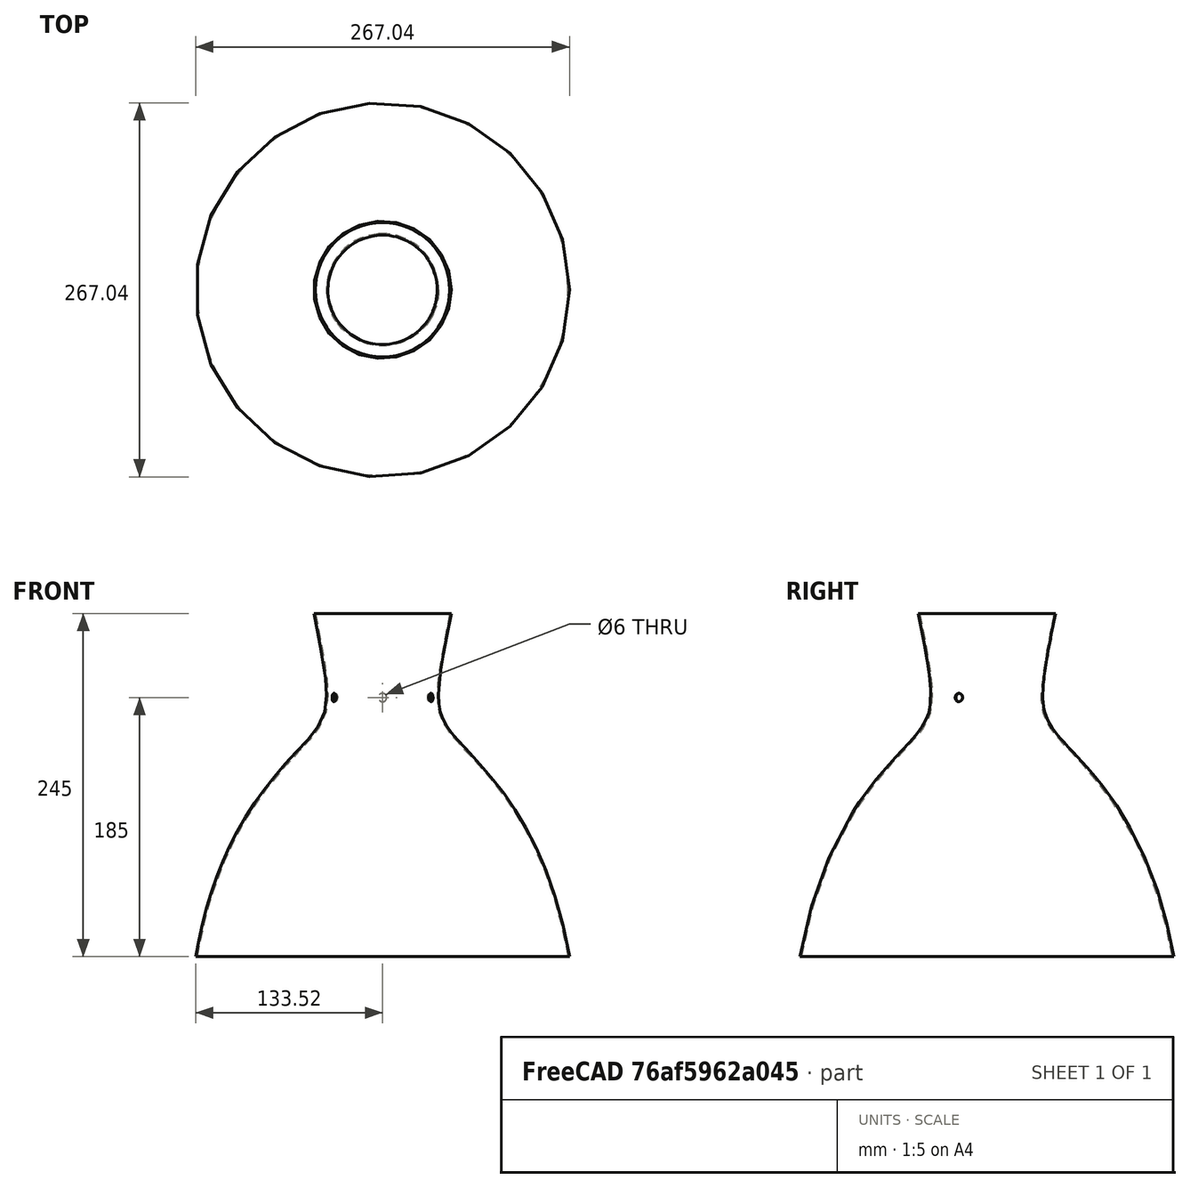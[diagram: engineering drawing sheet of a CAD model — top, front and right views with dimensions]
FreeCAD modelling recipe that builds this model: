
FCSTD DOCUMENT  (FreeCAD 0.20R29603 (Git))
Label: kitchen_lamp_shade_replacement_smaller
License: All rights reserved
LicenseURL: http://en.wikipedia.org/wiki/All_rights_reserved
objects: Sketcher::SketchObject×2, PartDesign::Revolution×1, PartDesign::Thickness×1, PartDesign::Pocket×1, PartDesign::PolarPattern×1, PartDesign::Body×1
note: 10 computed .brp shape members not serialized (recipe doc carries the construction recipe); baked Part::Feature solids carry a one-line shape summary decoded from their .brp

FEATURE [Sketcher::SketchObject] Sketch
  FullyConstrained = false
  MapMode = 5
  Placement = pos=(0,0,0) rot=(1,0,0;1.5708rad)
  Support = -> [XZ_Plane]
  sketch-geometry (14):
    g0: LineSegment StartX=0 StartY=0 StartZ=0 EndX=0 EndY=245 EndZ=0
    g1: LineSegment StartX=0 StartY=245 StartZ=0 EndX=48 EndY=245 EndZ=0
    g2: LineSegment StartX=0 StartY=0 StartZ=0 EndX=132.5 EndY=0 EndZ=0
    g3-g7: Circle x5 (B-spline internal-alignment scaffolding for g8; pole/knot coordinates omitted)
    g8: BSplineCurve PolesCount=5 KnotsCount=3 Degree=3 IsPeriodic=0
    g9: GeomPoint X=48 Y=245 Z=0
    g10: GeomPoint X=55.3881 Y=151.21 Z=0
    g11: GeomPoint X=132.5 Y=0 Z=0
    g12: GeomPoint X=35 Y=185 Z=0
    g13: LineSegment StartX=38.6274 StartY=231.38 StartZ=0 EndX=38.6274 EndY=147.717 EndZ=0
  constraints (23):
    c: Coincident(g0,g-1)
    c: PointOnObject(g0,g-2)
    c: Coincident(g1,g0)
    c: Horizontal(g1)
    c: Coincident(g2,g0)
    c: PointOnObject(g2,g-1)
    c: Weight(g3) = 1
    c: Coincident(g8,g1)
    c: Equal(g3, g4-g7) x4
    c: Coincident(g8,g2)
    c: InternalAlignment(g3-g7 -> g8) x5
    c: InternalAlignment(g9,g8)
    c: InternalAlignment(g10,g8)
    c: InternalAlignment(g11,g8)
    c: DistanceY(g0,g0) = 245  'height'
    c: DistanceX(g2,g2) = 132.5  'radius_bottom'
    c: DistanceX(g1,g1) = 48  'radius_top'
    c: Vertical(g5,g4)
    c: DistanceY(g5,g4) = 13
    c: DistanceX(g0,g4) = 35
    c: DistanceY(g12) = 185  'height_neck'
    c: Vertical(g13)
    c: Vertical(g12,g4)
FEATURE [PartDesign::Revolution] Revolution
  Angle = 360
  Axis = (0,-2e-16,1)
  Base = (0,0,0)
  Placement = pos=(0,0,0) rot=(1,0,0;1.5708rad)
  Profile = -> Sketch
  ReferenceAxis = -> Sketch [V_Axis]
  Reversed = true
FEATURE [Sketcher::SketchObject] Sketch001
  FullyConstrained = true
  MapMode = 5
  Placement = pos=(0,0,0) rot=(1,0,0;1.5708rad)
  Support = -> [XZ_Plane]
  expr: Constraints[1] = Sketch.Constraints.height_neck
  sketch-geometry (1):
    g0: Circle CenterX=0 CenterY=185 CenterZ=0 NormalX=0 NormalY=0 NormalZ=1 AngleXU=0 Radius=3
  constraints (3):
    c: PointOnObject(g0,g-2)
    c: DistanceY(g-1,g0) = 185
    c: Diameter(g0) = 6
FEATURE [PartDesign::Thickness] Thickness
  Base = -> Revolution [Face3,Face1]
  BaseFeature = -> Revolution
  Intersection = false
  Join = 0
  Mode = 0
  SupportTransform = false
  Value = 1
FEATURE [PartDesign::Pocket] Pocket
  BaseFeature = -> Thickness
  Direction = (0,1,2e-16)
  Length = 5
  Length2 = 5
  Profile = -> Sketch001
  ReferenceAxis = -> Sketch001 [N_Axis]
  Type = 1
FEATURE [PartDesign::PolarPattern] PolarPattern
  Angle = 360
  Axis = -> Z_Axis
  BaseFeature = -> Pocket
  Occurrences = 3
  Originals = -> [Pocket]
FEATURE [PartDesign::Body] Body
  Group = -> [Sketch,Revolution,Thickness,Sketch001,Pocket,PolarPattern]
  Origin = -> Origin
  Tip = -> PolarPattern
